# Revit family: Hager-GOLF-Surface_mounted-IP40-With_Cover-With_DIN-Hosted-CH-de
name_source: partatom
category: Electrical Equipment
units: mm (PartAtom-declared; Revit-internal decimal feet)

## family parameters
Cut with Voids When Loaded = No
Host = Face
Maintain Annotation Orientation = Yes
Panel Configuration = Two Columns, Circuits Across
Part Type = Panelboard
Room Calculation Point = No
Round Connector Dimension = Use Diameter
Shared = No

## types (18) — shared parameters
BC_MODEL_ID = 1539123
BC_OBJECT_ID = 512265
BC_OBJECT_VERSION = #44
Code hager = ADD-EC000214_EU
EF000003 - Montageart = Aufputz
EF000007 - Farbe = weiss
EF000024 - UV-beständig = No
EF000049 - Tiefe = 99 mm  [stored 0.324803 ft]
EF000116 - RAL-Nummer = 9010
EF000118 - Mit Montageplatte = No
EF001062 - EMV-Ausführung = No
EF001088 - Anbaumöglichkeit = Yes
EF001134 - DIN-Schiene = Yes
EF004462 - Art der Schliessung = sonstige
EF005474 - Schutzart (IP) = IP40
EF006306 - Mit Schloss = No
EF009212 - Ausführung Deckel = geschlossen
EF015941 - Signaldurchlassende Tür = Yes
ETIM class code = EC000214
ETIM class name = Small distribution board
HG000001-Anzahl der Spalten = 1
HG000002-Mit tür = Yes
HG000003-Bereich = GOLF
HG000005-Dicke = 2 mm  [stored 0.00656168 ft]
HG000006-Unterputz = No
HG000009-Doppelflügeligen Tür = No
HG000010-Asymmetrische Türen = No
HG000011-Leere Reihen von unten = No
HG000012-Türschwenkwinkel = 90.00°
HG000013-Tür links = No
HG000014-Tür rechts = Yes
HG000015-Sichtbarkeit der Türöffnung = Yes
HG000016-3D-Türsichtbarkeit = Yes
HG000017-Distanz zwischen den Polen = 18 mm  [stored 0.0590551 ft]
HG000060-RAL-number = 9010
HG000099-Onfly Template ID-de-CH = 507532
Manufacturer = Hager
Name = GOLF-Surface_mounted-IP40-With_Cover-With_DIN-CH
Name BIM&CO = Electricity
Name hager = ADD_Enclosures_EC000214
Uniformat = Low Tension Service & Dist.
Uniformat code = D501001
zero-valued in all types: Default Elevation, EF000218 - Einbautiefe, EF000332 - Einbauhöhe, EF000846 - Einbaubreite, EF001131 - Innentiefe, HG000007-Anzahl der leeren Spalten, HG000008-Anzahl der leeren Reihen

## per-type parameters (varying)
| type | BC_VARIANT_ID | EF000008 - Breite | EF000040 - Höhe | EF000266 - Anzahl der Reihen | EF002950 - Anzahl Teilungseinheiten | EF006244 - Transparenter Deckel/Tür | EF015776 - Erdungsklemmenblock | EF015777 - Neutralleiterklemmenblock | HG000004-Herstellerreferenz | HGEF000266-Anzahl der Reihen | HGEF0002950-Breite in Teilungseinheiten |
| GOLF-Surface_mounted_W138_H184_D99_4_Modular_Spacing-VS104PS | 1169097 | 138 mm  [stored 0.452756 ft] | 184 mm  [stored 0.603675 ft] | 1 | 4 | No | No | No | VS104PS | 1 | 4 |
| GOLF-Surface_mounted_W138_H184_D99_4_Modular_Spacing-VS104TS | 1169098 | 138 mm  [stored 0.452756 ft] | 184 mm  [stored 0.603675 ft] | 1 | 4 | Yes | No | No | VS104TS | 1 | 4 |
| GOLF-Surface_mounted_W210_H184_D99_8_Modular_Spacing-VS108TS | 1169099 | 210 mm  [stored 0.688976 ft] | 184 mm  [stored 0.603675 ft] | 1 | 8 | Yes | No | No | VS108TS | 1 | 8 |
| GOLF-Surface_mounted_W282_H252_D99_12_Modular_Spacing-VS112PS | 1169100 | 282 mm | 252 mm  [stored 0.826772 ft] | 1 | 12 | No | Yes | Yes | VS112PS | 1 | 12 |
| GOLF-Surface_mounted_W282_H252_D99_12_Modular_Spacing-VS112TS | 1169101 | 282 mm | 252 mm  [stored 0.826772 ft] | 1 | 12 | Yes | Yes | Yes | VS112TS | 1 | 12 |
| GOLF-Surface_mounted_W390_H252_D99_18_Modular_Spacing-VS118PS | 1169102 | 390 mm  [stored 1.27953 ft] | 252 mm  [stored 0.826772 ft] | 1 | 18 | No | Yes | Yes | VS118PS | 1 | 18 |
| GOLF-Surface_mounted_W390_H252_D99_18_Modular_Spacing-VS118TS | 1169103 | 390 mm  [stored 1.27953 ft] | 252 mm  [stored 0.826772 ft] | 1 | 18 | Yes | Yes | Yes | VS118TS | 1 | 18 |
| GOLF-Surface_mounted_W462_H252_D99_22_Modular_Spacing-VS122PS | 1169104 | 462 mm  [stored 1.51575 ft] | 252 mm  [stored 0.826772 ft] | 1 | 22 | No | Yes | Yes | VS122PS | 1 | 22 |
| GOLF-Surface_mounted_W282_H377_D99_12_Modular_Spacing-VS212PS | 1169105 | 282 mm | 377 mm  [stored 1.23688 ft] | 2 | 12 | No | Yes | Yes | VS212PS | 2 | 12 |
| GOLF-Surface_mounted_W282_H377_D99_12_Modular_Spacing-VS212TS | 1169106 | 282 mm | 377 mm  [stored 1.23688 ft] | 2 | 12 | Yes | Yes | Yes | VS212TS | 2 | 12 |
| GOLF-Surface_mounted_W390_H377_D99_18_Modular_Spacing-VS218PS | 1169107 | 390 mm  [stored 1.27953 ft] | 377 mm  [stored 1.23688 ft] | 2 | 18 | No | Yes | Yes | VS218PS | 2 | 18 |
| GOLF-Surface_mounted_W390_H377_D99_18_Modular_Spacing-VS218TS | 1169108 | 390 mm  [stored 1.27953 ft] | 377 mm  [stored 1.23688 ft] | 2 | 18 | Yes | Yes | Yes | VS218TS | 2 | 18 |
| GOLF-Surface_mounted_W282_H500_D99_12_Modular_Spacing-VS312PS | 1169109 | 282 mm | 500 mm  [stored 1.64042 ft] | 3 | 12 | No | Yes | Yes | VS312PS | 3 | 12 |
| GOLF-Surface_mounted_W390_H500_D99_18_Modular_Spacing-VS318PS | 1169110 | 390 mm  [stored 1.27953 ft] | 500 mm  [stored 1.64042 ft] | 3 | 18 | No | Yes | Yes | VS318PS | 3 | 18 |
| GOLF-Surface_mounted_W390_H500_D99_18_Modular_Spacing-VS318TS | 1169111 | 390 mm  [stored 1.27953 ft] | 500 mm  [stored 1.64042 ft] | 3 | 18 | Yes | Yes | Yes | VS318TS | 3 | 18 |
| GOLF-Surface_mounted_W282_H647_D99_12_Modular_Spacing-VS412PS | 1169112 | 282 mm | 647 mm  [stored 2.1227 ft] | 4 | 12 | No | Yes | Yes | VS412PS | 4 | 12 |
| GOLF-Surface_mounted_W390_H647_D99_18_Modular_Spacing-VS418PS | 1169113 | 390 mm  [stored 1.27953 ft] | 647 mm  [stored 2.1227 ft] | 4 | 18 | No | Yes | Yes | VS418PS | 4 | 18 |
| GOLF-Surface_mounted_W390_H647_D99_18_Modular_Spacing-VS418TS | 1169114 | 390 mm  [stored 1.27953 ft] | 647 mm  [stored 2.1227 ft] | 4 | 18 | Yes | Yes | Yes | VS418TS | 4 | 18 |

note: column(s) folded — value = type name in every type: Reference

note: [stored X ft] marks values corroborated as IEEE doubles in the binary element streams (Revit-internal decimal feet)

## geometry (parser evidence)
native form markers: Sweep x14
no freeform markers — native parametric forms only
